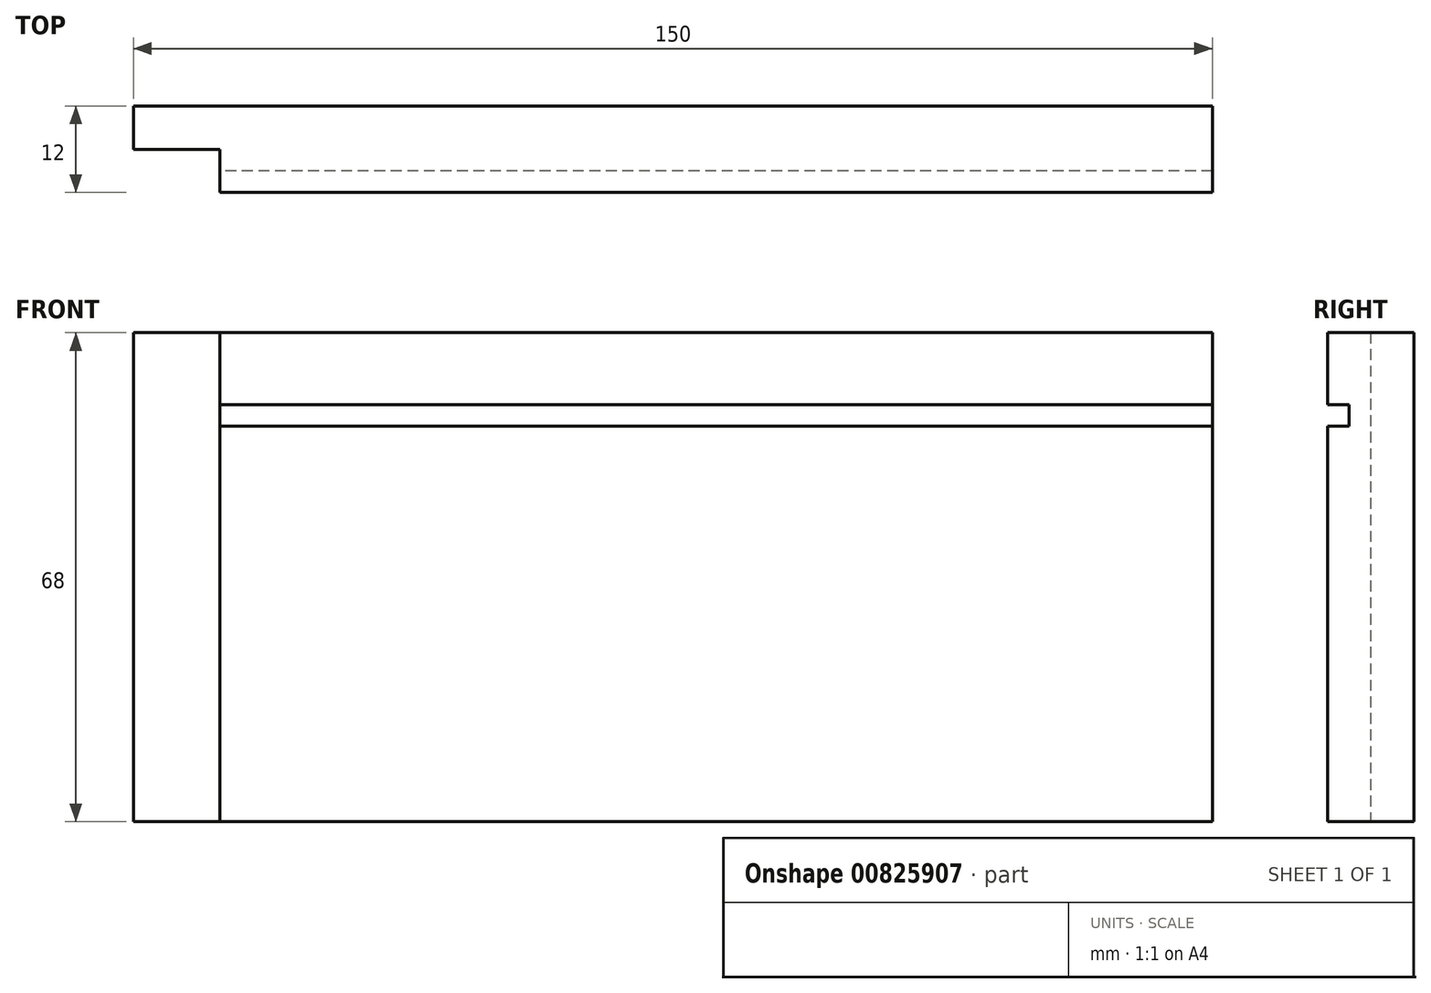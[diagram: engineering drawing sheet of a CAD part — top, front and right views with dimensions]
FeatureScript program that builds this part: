
annotation { "Feature Type Name" : "Feature", "Feature Type Description" : "" }
export const myFeature = defineFeature(function(context is Context, id is Id, definition is map)
    precondition{}
    {
        {
            var Q0;
            Q0=qCreatedBy(makeId("Right.planeOp"),FACE);
            var sketch = newSketch(context, id + "F0", { "sketchPlane" : qUnion([Q0])});
            skLineSegment(sketch, "E0.bottom", {"start": v(0, 0) * mm, "end": v(12, 0) * mm});
            skLineSegment(sketch, "E0.top", {"start": v(0, 68) * mm, "end": v(12, 68) * mm});
            skLineSegment(sketch, "E0.left", {"start": v(0, 0) * mm, "end": v(0, 68) * mm});
            skLineSegment(sketch, "E0.right", {"start": v(12, 0) * mm, "end": v(12, 68) * mm});
            skLineSegment(sketch, "E1.bottom", {"start": v(0, 55) * mm, "end": v(3, 55) * mm});
            skLineSegment(sketch, "E1.top", {"start": v(0, 58) * mm, "end": v(3, 58) * mm});
            skLineSegment(sketch, "E1.left", {"start": v(0, 55) * mm, "end": v(0, 58) * mm});
            skLineSegment(sketch, "E1.right", {"start": v(3, 55) * mm, "end": v(3, 58) * mm});
            skLineSegment(sketch, "E2", {"start": v(0, 68) * mm, "end": v(0, 58) * mm});
            skSolve(sketch);
        }
        {
            var Q0;
            Q0=makeQuery(id+"F0.imprint","IMPRINT",FACE,{"disambiguationData":[TD([[makeQuery(id+"F0.imprint","IMPRINT",EDGE,{"derivedFrom":sQuery(id+"F0.wireOp",EDGE,"E0.bottom")}),1.0]])]});
            extrude(context, id + "F1", {"entities" : qUnion([Q0]), "depth" : 150 * mm, "offsetDistance" : 25 * mm});
        }
        {
            var Q0;
            Q0=qCreatedBy(makeId("Top.planeOp"),FACE);
            var sketch = newSketch(context, id + "F2", { "sketchPlane" : qUnion([Q0])});
            skLineSegment(sketch, "E3.bottom", {"start": v(0, 0) * mm, "end": v(12, 0) * mm});
            skLineSegment(sketch, "E3.top", {"start": v(0, 6) * mm, "end": v(12, 6) * mm});
            skLineSegment(sketch, "E3.left", {"start": v(0, 0) * mm, "end": v(0, 6) * mm});
            skLineSegment(sketch, "E3.right", {"start": v(12, 0) * mm, "end": v(12, 6) * mm});
            skSolve(sketch);
        }
        {
            var Q0;
            Q0 = qSketchRegion(id + "F2", true);
            extrude(context, id + "F3", {"entities" : qUnion([Q0]), "operationType" : NewBodyOperationType.REMOVE, "oppositeDirection" : true, "depth" : -68 * mm, "offsetDistance" : 25 * mm});
        }
    });
